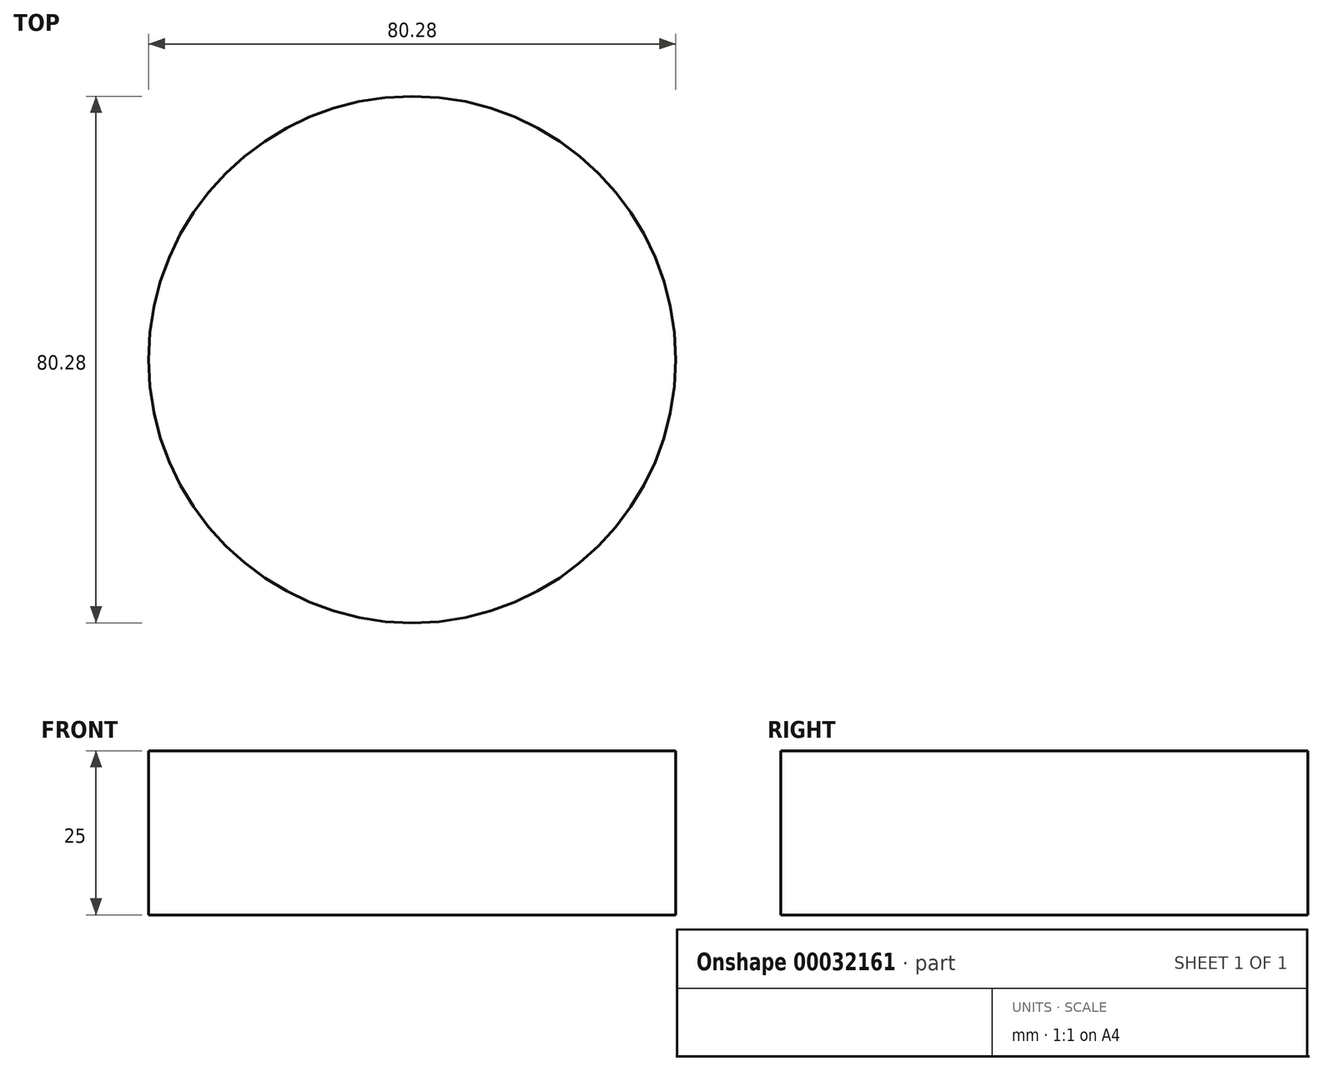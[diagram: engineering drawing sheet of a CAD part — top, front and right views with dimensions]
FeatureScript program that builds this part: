
annotation { "Feature Type Name" : "Feature", "Feature Type Description" : "" }
export const myFeature = defineFeature(function(context is Context, id is Id, definition is map)
    precondition{}
    {
        {
            var Q0;
            Q0=qCreatedBy(makeId("Top.planeOp"),FACE);
            var sketch = newSketch(context, id + "F0", { "sketchPlane" : qUnion([Q0])});
            skCircle(sketch, "E0", {"center": v(0, 0) * mm, "radius": 40.14 * mm});
            skSolve(sketch);
        }
        {
            var Q0;
            Q0 = qSketchRegion(id + "F0", true);
            extrude(context, id + "F1", {"entities" : qUnion([Q0]), "depth" : 25 * mm});
        }
    });
